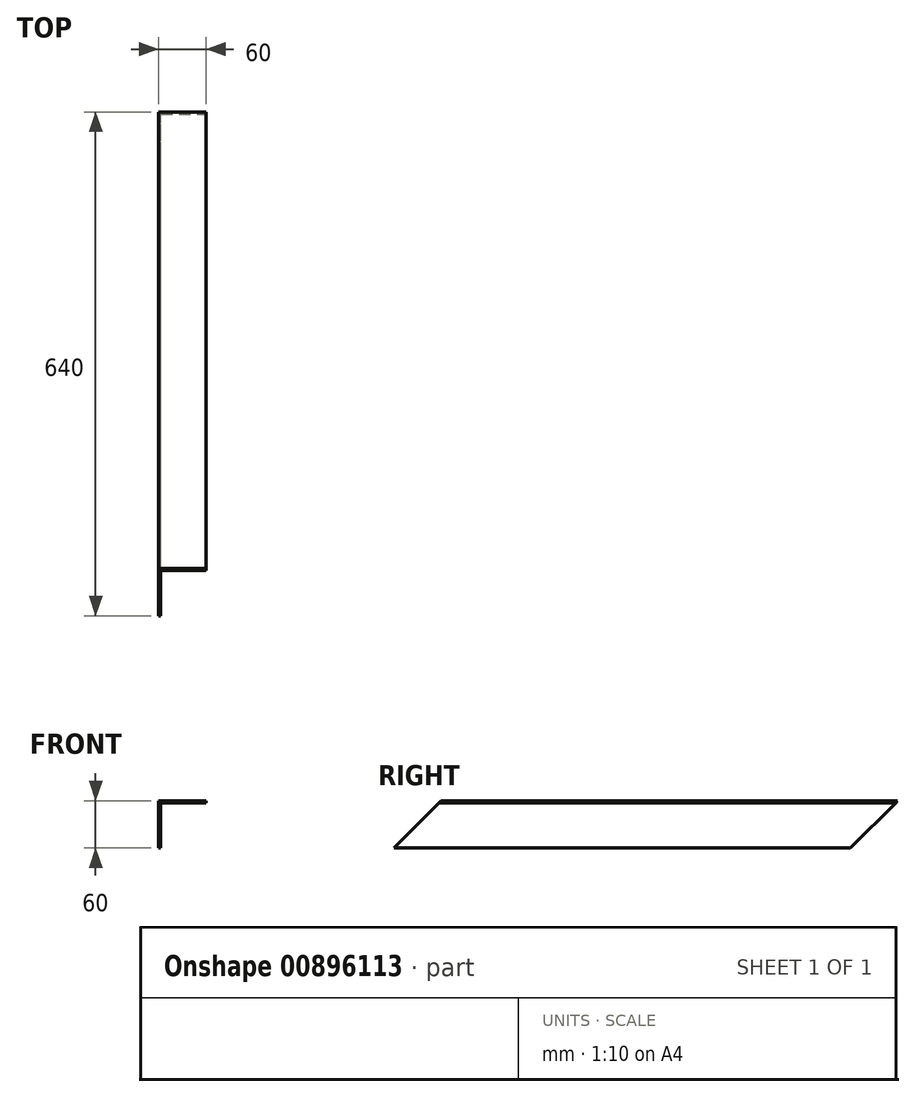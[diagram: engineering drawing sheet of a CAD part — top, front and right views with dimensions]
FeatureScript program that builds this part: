
annotation { "Feature Type Name" : "Feature", "Feature Type Description" : "" }
export const myFeature = defineFeature(function(context is Context, id is Id, definition is map)
    precondition{}
    {
        {
            var Q0;
            Q0=qCreatedBy(makeId("Front.planeOp"),FACE);
            var sketch = newSketch(context, id + "F0", { "sketchPlane" : qUnion([Q0])});
            skLineSegment(sketch, "E0", {"start": v(0, 0) * mm, "end": v(60, 0) * mm});
            skLineSegment(sketch, "E1", {"start": v(60, 0) * mm, "end": v(60, -2.5) * mm});
            skLineSegment(sketch, "E2", {"start": v(60, -2.5) * mm, "end": v(2.5, -2.5) * mm});
            skLineSegment(sketch, "E3", {"start": v(2.5, -2.5) * mm, "end": v(2.5, -60) * mm});
            skLineSegment(sketch, "E4", {"start": v(2.5, -60) * mm, "end": v(0, -60) * mm});
            skLineSegment(sketch, "E5", {"start": v(0, -60) * mm, "end": v(0, 0) * mm});
            skSolve(sketch);
        }
        {
            var Q0;
            Q0=qSketchRegion(id+"F0",true);
            extrude(context, id + "F1", {"entities" : qUnion([Q0]), "depth" : 640 * mm, "offsetDistance" : 25 * mm});
        }
        {
            var Q0;
            Q0=makeQuery(id+"F1.opExtrude","SWEPT_FACE",FACE,{"disambiguationData":[OSD([sQuery(id+"F0.wireOp",EDGE,"E5")])]});
            var sketch = newSketch(context, id + "F2", { "sketchPlane" : qUnion([Q0])});
            skLineSegment(sketch, "E6", {"start": v(0, 0) * mm, "end": v(60, -60) * mm});
            skLineSegment(sketch, "E7", {"start": v(60, -60) * mm, "end": v(0, -60) * mm});
            skLineSegment(sketch, "E8", {"start": v(0, -60) * mm, "end": v(0, 0) * mm});
            skLineSegment(sketch, "E9", {"start": v(640, -60) * mm, "end": v(580, 0) * mm});
            skLineSegment(sketch, "E10", {"start": v(580, 0) * mm, "end": v(640, 0) * mm});
            skLineSegment(sketch, "E11", {"start": v(640, 0) * mm, "end": v(640, -60) * mm});
            skSolve(sketch);
        }
        {
            var Q0;
            Q0 = qSketchRegion(id + "F2", true);
            extrude(context, id + "F3", {"entities" : qUnion([Q0]), "operationType" : NewBodyOperationType.REMOVE, "endBound" : BoundingType.THROUGH_ALL, "oppositeDirection" : true, "depth" : 25 * mm, "offsetDistance" : 25 * mm});
        }
    });
